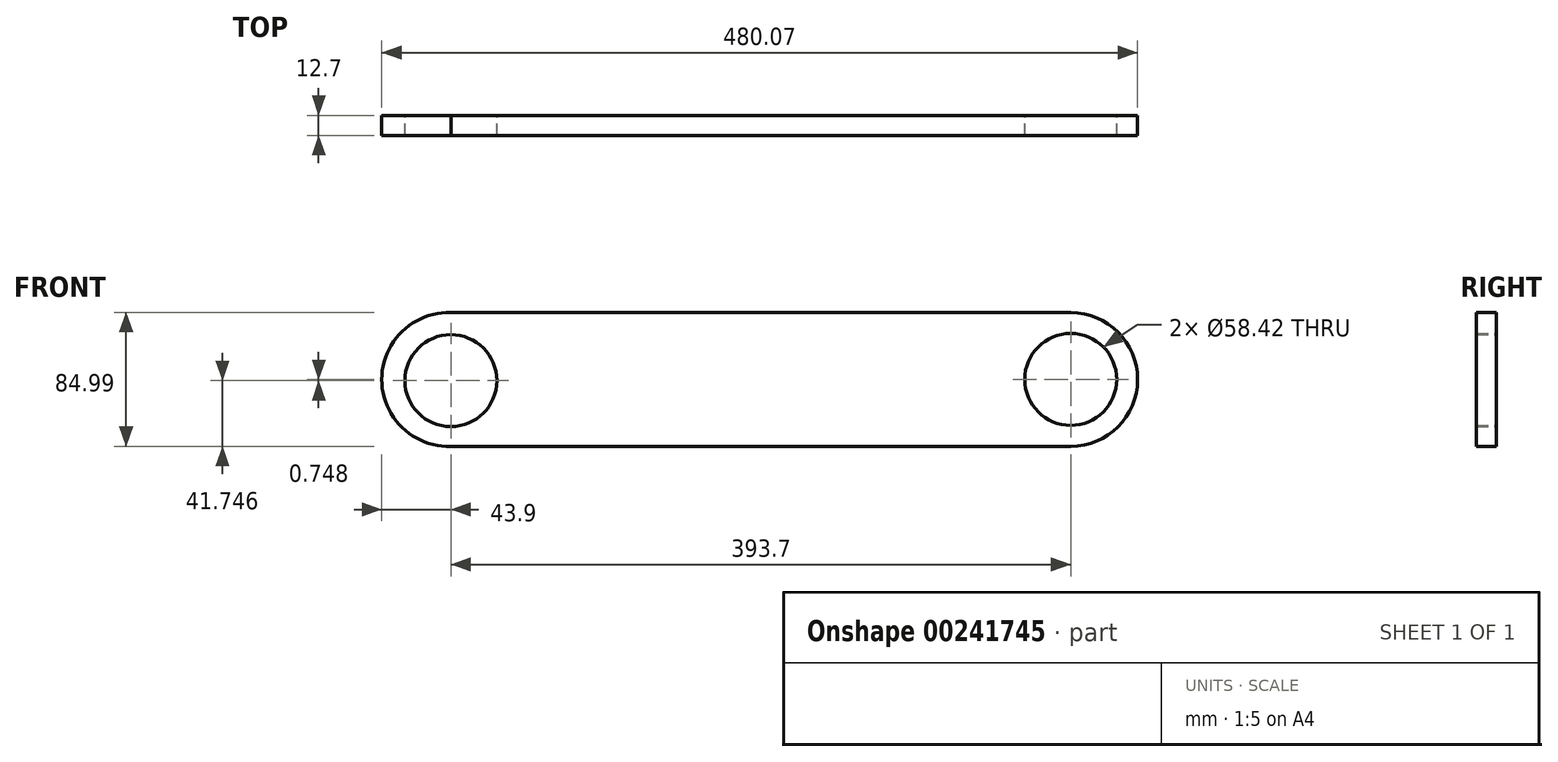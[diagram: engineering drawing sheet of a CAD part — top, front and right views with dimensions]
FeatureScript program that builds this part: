
annotation { "Feature Type Name" : "Feature", "Feature Type Description" : "" }
export const myFeature = defineFeature(function(context is Context, id is Id, definition is map)
    precondition{}
    {
        {
            var Q0;
            Q0=qCreatedBy(makeId("Front.planeOp"),FACE);
            var sketch = newSketch(context, id + "F0", { "sketchPlane" : qUnion([Q0])});
            skCircle(sketch, "E0", {"center": v(-64.61, 5.89) * mm, "radius": 29.21 * mm});
            skArc(sketch, "E1", {"start": v(-64.61, 49.1) * mm, "mid": v(-108.51, 6.63) * mm, "end": v(-64.61, -35.84) * mm});
            skLineSegment(sketch, "E2", {"start": v(-64.61, -35.84) * mm, "end": v(329.09, -35.84) * mm});
            skLineSegment(sketch, "E3", {"start": v(-64.61, 49.1) * mm, "end": v(329.09, 49.1) * mm});
            skCircle(sketch, "E4", {"center": v(329.09, 6.63) * mm, "radius": 29.21 * mm});
            skArc(sketch, "E5", {"start": v(329.09, -35.84) * mm, "mid": v(371.56, 6.63) * mm, "end": v(329.09, 49.1) * mm});
            skSolve(sketch);
        }
        {
            var Q0;
            Q0 = qSketchRegion(id + "F0", true);
            extrude(context, id + "F1", {"entities" : qUnion([Q0]), "depth" : 12.7 * mm});
        }
    });
